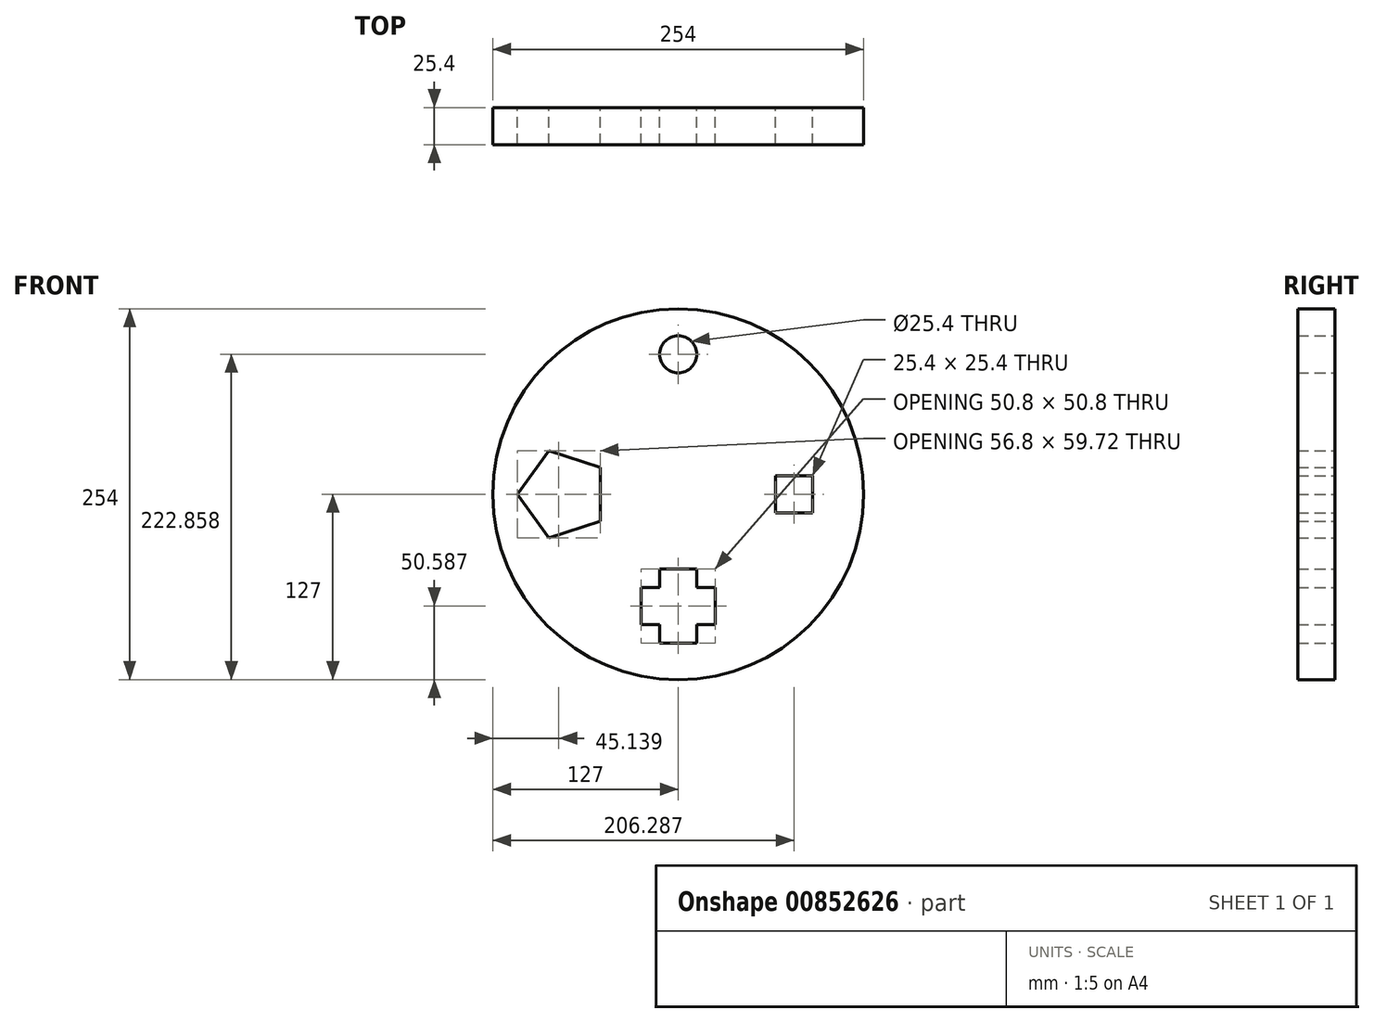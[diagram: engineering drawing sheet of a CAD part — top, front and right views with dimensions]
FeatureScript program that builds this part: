
annotation { "Feature Type Name" : "Feature", "Feature Type Description" : "" }
export const myFeature = defineFeature(function(context is Context, id is Id, definition is map)
    precondition{}
    {
        {
            var Q0;
            Q0=qCreatedBy(makeId("Front.planeOp"),FACE);
            var sketch = newSketch(context, id + "F0", { "sketchPlane" : qUnion([Q0])});
            skCircle(sketch, "E0", {"center": v(0, 0) * mm, "radius": 127 * mm});
            skCircle(sketch, "E1", {"center": v(0, 95.86) * mm, "radius": 12.7 * mm});
            skLineSegment(sketch, "E2.bottom", {"start": v(91.99, -12.7) * mm, "end": v(66.59, -12.7) * mm});
            skLineSegment(sketch, "E2.top", {"start": v(91.99, 12.7) * mm, "end": v(66.59, 12.7) * mm});
            skLineSegment(sketch, "E2.left", {"start": v(91.99, -12.7) * mm, "end": v(91.99, 12.7) * mm});
            skLineSegment(sketch, "E2.right", {"start": v(66.59, -12.7) * mm, "end": v(66.59, 12.7) * mm});
            skPoint(sketch, "E2.middle", {"position": v(79.29, 0) * mm});
            skCircle(sketch, "E3.cCircle", {"center": v(-78.86, 0) * mm, "radius": 25.4 * mm, "construction": true});
            skLineSegment(sketch, "E3.0", {"start": v(-53.46, 18.45) * mm, "end": v(-53.46, -18.45) * mm});
            skLineSegment(sketch, "E3.1", {"start": v(-53.46, -18.45) * mm, "end": v(-88.56, -29.86) * mm});
            skLineSegment(sketch, "E3.2", {"start": v(-88.56, -29.86) * mm, "end": v(-110.26, 0) * mm});
            skLineSegment(sketch, "E3.3", {"start": v(-110.26, 0) * mm, "end": v(-88.56, 29.86) * mm});
            skLineSegment(sketch, "E3.4", {"start": v(-88.56, 29.86) * mm, "end": v(-53.46, 18.45) * mm});
            skPoint(sketch, "E3.0.midPoint", {"position": v(-53.46, 0) * mm});
            skLineSegment(sketch, "E4.bottom", {"start": v(25.4, -89.11) * mm, "end": v(-25.4, -89.11) * mm});
            skLineSegment(sketch, "E4.top", {"start": v(25.4, -63.71) * mm, "end": v(-25.4, -63.71) * mm});
            skLineSegment(sketch, "E4.left", {"start": v(25.4, -89.11) * mm, "end": v(25.4, -63.71) * mm});
            skLineSegment(sketch, "E4.right", {"start": v(-25.4, -89.11) * mm, "end": v(-25.4, -63.71) * mm});
            skPoint(sketch, "E4.middle", {"position": v(0, -76.41) * mm});
            skLineSegment(sketch, "E5.bottom", {"start": v(-12.7, -51.01) * mm, "end": v(12.7, -51.01) * mm});
            skLineSegment(sketch, "E5.top", {"start": v(-12.7, -101.81) * mm, "end": v(12.7, -101.81) * mm});
            skLineSegment(sketch, "E5.left", {"start": v(-12.7, -51.01) * mm, "end": v(-12.7, -101.81) * mm});
            skLineSegment(sketch, "E5.right", {"start": v(12.7, -51.01) * mm, "end": v(12.7, -101.81) * mm});
            skSolve(sketch);
        }
        {
            var Q0;
            Q0=makeQuery(id+"F0.imprint","IMPRINT",FACE,{"disambiguationData":[TD([[makeQuery(id+"F0.imprint","IMPRINT",EDGE,{"derivedFrom":sQuery(id+"F0.wireOp",EDGE,"E0")}),1.0]])]});
            extrude(context, id + "F1", {"entities" : qUnion([Q0]), "endBound" : BoundingType.SYMMETRIC, "depth" : 25.4 * mm, "offsetDistance" : 25.4 * mm});
        }
    });
